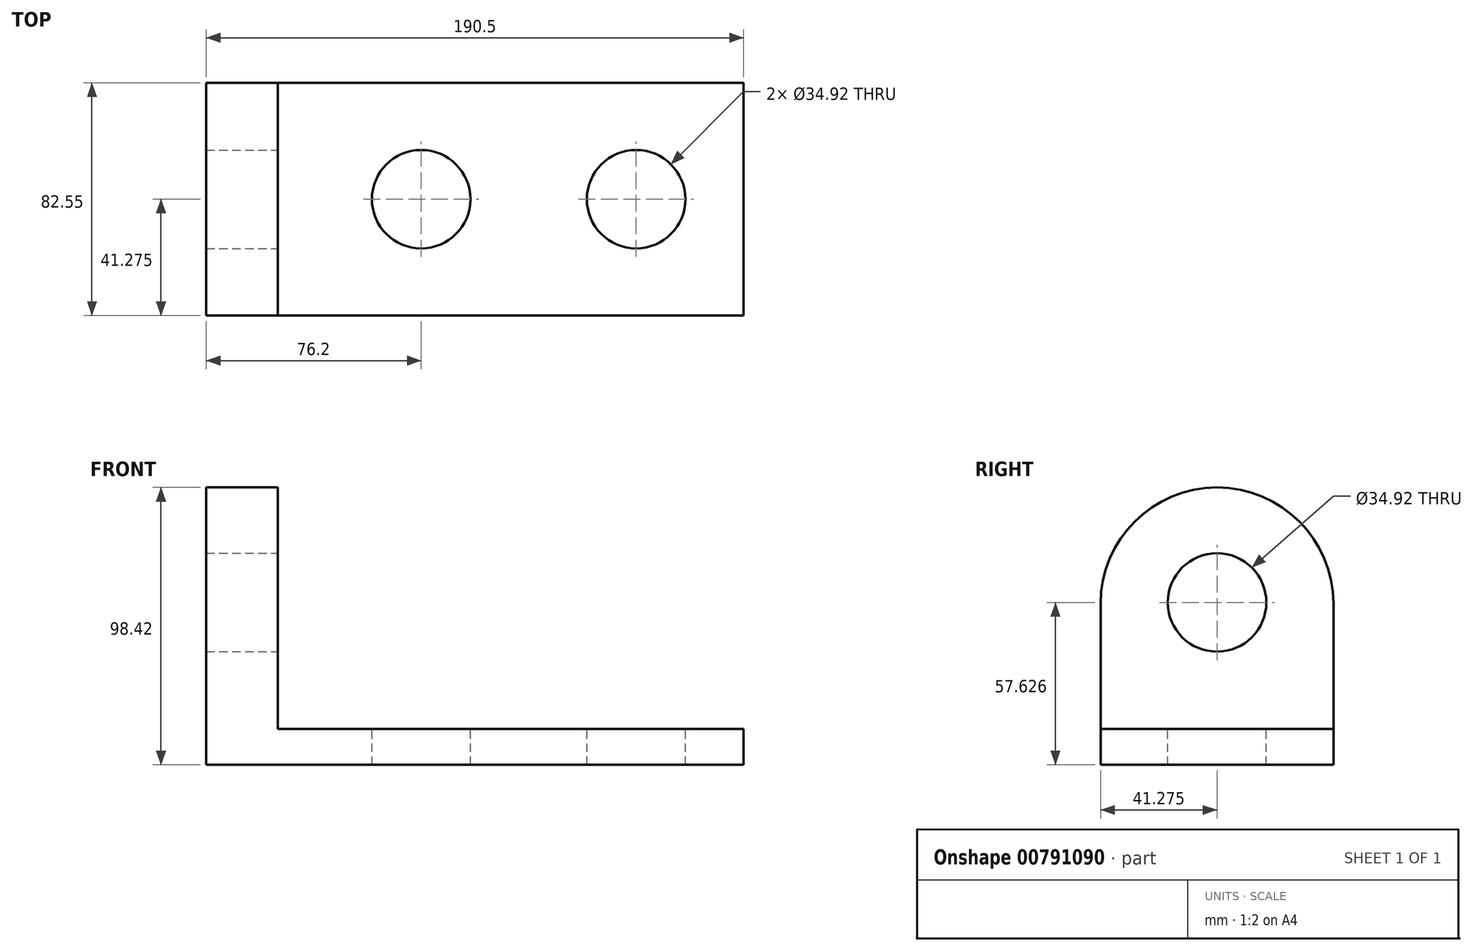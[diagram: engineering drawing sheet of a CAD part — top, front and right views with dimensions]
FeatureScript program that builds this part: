
annotation { "Feature Type Name" : "Feature", "Feature Type Description" : "" }
export const myFeature = defineFeature(function(context is Context, id is Id, definition is map)
    precondition{}
    {
        {
            var Q0;
            Q0=qCreatedBy(makeId("Front.planeOp"),FACE);
            var sketch = newSketch(context, id + "F0", { "sketchPlane" : qUnion([Q0])});
            skLineSegment(sketch, "E0", {"start": v(0, 0) * mm, "end": v(190.5, 0) * mm});
            skLineSegment(sketch, "E1", {"start": v(190.5, 0) * mm, "end": v(190.5, 12.7) * mm});
            skLineSegment(sketch, "E2", {"start": v(190.5, 12.7) * mm, "end": v(25.4, 12.7) * mm});
            skLineSegment(sketch, "E3", {"start": v(25.4, 12.7) * mm, "end": v(25.4, 114.3) * mm});
            skLineSegment(sketch, "E4", {"start": v(25.4, 114.3) * mm, "end": v(0, 114.3) * mm});
            skLineSegment(sketch, "E5", {"start": v(0, 114.3) * mm, "end": v(0, 0) * mm});
            skSolve(sketch);
        }
        {
            var Q0;
            Q0 = qSketchRegion(id + "F0", true);
            extrude(context, id + "F1", {"entities" : qUnion([Q0]), "oppositeDirection" : true, "depth" : 82.55 * mm, "offsetDistance" : 25.4 * mm});
        }
        {
            var Q0;
            Q0=makeQuery(id+"F1.opExtrude","SWEPT_FACE",FACE,{"disambiguationData":[OSD([sQuery(id+"F0.wireOp",EDGE,"E2")])]});
            var sketch = newSketch(context, id + "F2", { "sketchPlane" : qUnion([Q0])});
            skCircle(sketch, "E6", {"center": v(76.2, 41.28) * mm, "radius": 17.46 * mm});
            skCircle(sketch, "E7", {"center": v(152.4, 41.28) * mm, "radius": 17.46 * mm});
            skSolve(sketch);
        }
        {
            var Q0;
            Q0 = qSketchRegion(id + "F2", true);
            extrude(context, id + "F3", {"entities" : qUnion([Q0]), "operationType" : NewBodyOperationType.REMOVE, "oppositeDirection" : true, "depth" : 12.7 * mm, "offsetDistance" : 25.4 * mm});
        }
        {
            var Q0;
            Q0=makeQuery(id+"F1.opExtrude","SWEPT_FACE",FACE,{"disambiguationData":[OSD([sQuery(id+"F0.wireOp",EDGE,"E3")])]});
            var sketch = newSketch(context, id + "F4", { "sketchPlane" : qUnion([Q0])});
            skSolve(sketch);
        }
        {
            var Q0;
            Q0=makeQuery(id+"F1.opExtrude","SWEPT_FACE",FACE,{"disambiguationData":[OSD([sQuery(id+"F0.wireOp",EDGE,"E5")])]});
            var sketch = newSketch(context, id + "F5", { "sketchPlane" : qUnion([Q0])});
            skArc(sketch, "E8", {"start": v(0, 57.15) * mm, "mid": v(-41.28, 98.43) * mm, "end": v(-82.55, 57.15) * mm});
            skSolve(sketch);
        }
        {
            var Q0;
            {var subQ0=sQuery(id+"F5.wireOp",EDGE,"E8");Q0=makeQuery(id+"F5.imprint","IMPRINT",FACE,{"disambiguationData":[TD([[makeQuery(id+"F5.imprint","IMPRINT",EDGE,{"derivedFrom":subQ0}),-1.0]])]});}
            extrude(context, id + "F6", {"entities" : qUnion([Q0]), "operationType" : NewBodyOperationType.REMOVE, "oppositeDirection" : true, "depth" : 25.4 * mm, "offsetDistance" : 25.4 * mm});
        }
        {
            var Q0;
            {var subQ0=sQuery(id+"F0.wireOp",EDGE,"E3");Q0=makeQuery(id+"F4.imprint","IMPRINT",FACE,{"disambiguationData":[TD([[makeQuery(id+"F4.imprint","IMPRINT",EDGE,{"derivedFrom":makeQuery(id+"F1.opExtrude","CAP_EDGE",EDGE,{"disambiguationData":[OSD([subQ0])],"isStart":true})}),-1.0]])]});}
            var sketch = newSketch(context, id + "F7", { "sketchPlane" : qUnion([Q0])});
            skCircle(sketch, "E9", {"center": v(41.28, 57.63) * mm, "radius": 17.46 * mm});
            skSolve(sketch);
        }
        {
            var Q0;
            Q0 = qSketchRegion(id + "F7", true);
            extrude(context, id + "F8", {"entities" : qUnion([Q0]), "operationType" : NewBodyOperationType.REMOVE, "endBound" : BoundingType.UP_TO_NEXT, "oppositeDirection" : true, "depth" : 25.4 * mm, "offsetDistance" : 25.4 * mm});
        }
    });
